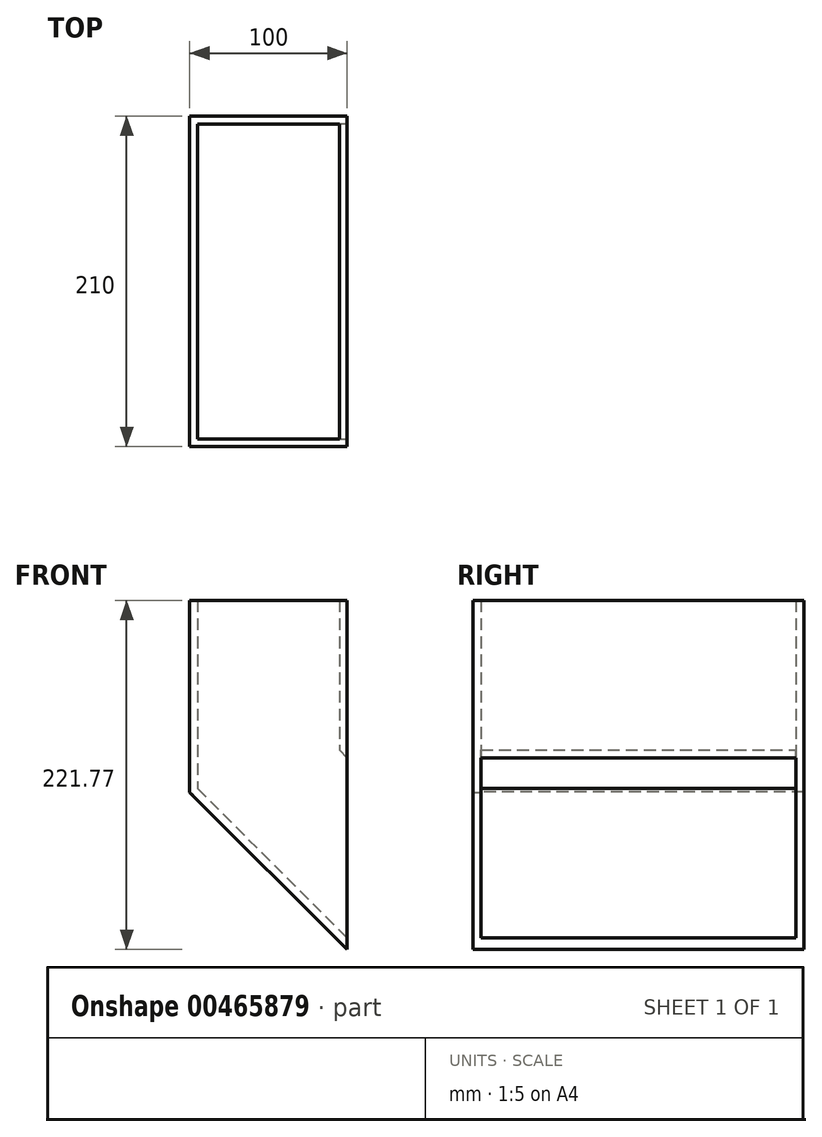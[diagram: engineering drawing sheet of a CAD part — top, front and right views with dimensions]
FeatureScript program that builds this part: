
annotation { "Feature Type Name" : "Feature", "Feature Type Description" : "" }
export const myFeature = defineFeature(function(context is Context, id is Id, definition is map)
    precondition{}
    {
        {
            var Q0;
            Q0=qCreatedBy(makeId("Front.planeOp"),FACE);
            var sketch = newSketch(context, id + "F0", { "sketchPlane" : qUnion([Q0])});
            skLineSegment(sketch, "E0", {"start": v(0, 0) * mm, "end": v(-200, 0) * mm, "construction": true});
            skLineSegment(sketch, "E1", {"start": v(0, 0) * mm, "end": v(-60.81, -60.81) * mm, "construction": true});
            skLineSegment(sketch, "E2", {"start": v(-100, 0) * mm, "end": v(-100, -77.94) * mm});
            skLineSegment(sketch, "E3", {"start": v(-60.81, -60.81) * mm, "end": v(-100, -21.62) * mm, "construction": true});
            skLineSegment(sketch, "E4", {"start": v(-100, 0) * mm, "end": v(-100, 200) * mm});
            skLineSegment(sketch, "E5", {"start": v(0, 0) * mm, "end": v(-100, 100) * mm, "construction": true});
            skLineSegment(sketch, "E6", {"start": v(-100, 107.07) * mm, "end": v(0, 7.07) * mm, "construction": true});
            skLineSegment(sketch, "E7", {"start": v(-100, -21.62) * mm, "end": v(-200, 78.38) * mm});
            skLineSegment(sketch, "E8", {"start": v(0, 0) * mm, "end": v(0, 200) * mm, "construction": true});
            skLineSegment(sketch, "E9", {"start": v(0, 200) * mm, "end": v(-200, 200) * mm});
            skLineSegment(sketch, "E10", {"start": v(-200, 78.38) * mm, "end": v(-200, 200) * mm});
            skLineSegment(sketch, "E11", {"start": v(-195, 200) * mm, "end": v(-195, 80.45) * mm});
            skLineSegment(sketch, "E12", {"start": v(-195, 80.45) * mm, "end": v(-100, -14.55) * mm});
            skLineSegment(sketch, "E13", {"start": v(-105, 200) * mm, "end": v(-105, 105) * mm});
            skLineSegment(sketch, "E14", {"start": v(-100, 100) * mm, "end": v(-105, 105) * mm});
            skSolve(sketch);
        }
        {
            var Q0;
            Q0 = qSketchRegion(id + "F0", true);
            extrude(context, id + "F1", {"entities" : qUnion([Q0]), "oppositeDirection" : true, "depth" : 5 * mm});
        }
        {
            var Q0;
            {var subQ3=sQuery(id+"F0.wireOp",EDGE,"E7");Q0=makeQuery(id+"F0.imprint","IMPRINT",FACE,{"disambiguationData":[TD([[makeQuery(id+"F0.imprint","IMPRINT",EDGE,{"derivedFrom":subQ3}),-1.0]])]});}
            var Q1;
            {var subQ4=sQuery(id+"F0.wireOp",EDGE,"E13");Q1=makeQuery(id+"F0.imprint","IMPRINT",FACE,{"disambiguationData":[TD([[makeQuery(id+"F0.imprint","IMPRINT",EDGE,{"derivedFrom":subQ4}),1.0]])]});}
            extrude(context, id + "F2", {"entities" : qUnion([Q0, Q1]), "operationType" : NewBodyOperationType.ADD, "depth" : 200 * mm});
        }
        {
            var Q0;
            {var subQ0=sQuery(id+"F0.wireOp",EDGE,"E11");Q0=makeQuery(id+"F0.imprint","IMPRINT",FACE,{"disambiguationData":[TD([[makeQuery(id+"F0.imprint","IMPRINT",EDGE,{"derivedFrom":subQ0}),1.0]])]});}
            cPlane(context, id + "F3", {"entities" : qUnion([Q0]), "cplaneType" : CPlaneType.OFFSET, "offset" : 200 * mm, "width" : 150 * mm, "height" : 150 * mm});
        }
        {
            var Q0;
            Q0=qCreatedBy(id+"F3.planeOp",FACE);
            var sketch = newSketch(context, id + "F4", { "sketchPlane" : qUnion([Q0])});
            skLineSegment(sketch, "E15", {"start": v(0, 0) * mm, "end": v(0, 200) * mm, "construction": true});
            skLineSegment(sketch, "E16", {"start": v(0, 200) * mm, "end": v(-200, 200) * mm});
            skLineSegment(sketch, "E17", {"start": v(-200, 200) * mm, "end": v(-200, 77.86) * mm});
            skLineSegment(sketch, "E18", {"start": v(0, 0) * mm, "end": v(-60.81, -60.81) * mm});
            skLineSegment(sketch, "E19", {"start": v(-60.81, -60.81) * mm, "end": v(-200, 77.86) * mm});
            skLineSegment(sketch, "E20", {"start": v(-100, 200) * mm, "end": v(-100, -21.77) * mm});
            skPoint(sketch, "E20.endSnap0", {"position": v(-100, 200) * mm});
            skSolve(sketch);
        }
        {
            var Q0;
            Q0 = qSketchRegion(id + "F4", true);
            extrude(context, id + "F5", {"entities" : qUnion([Q0]), "operationType" : NewBodyOperationType.ADD, "depth" : 5 * mm});
        }
    });
